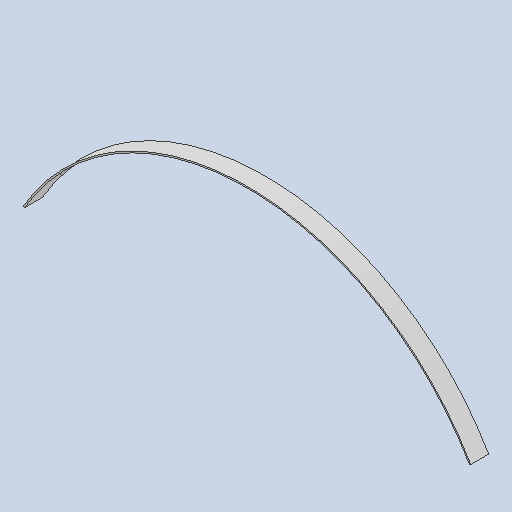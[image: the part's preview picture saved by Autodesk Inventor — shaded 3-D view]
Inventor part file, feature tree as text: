
AUTODESK INVENTOR PART (.ipt)
format: ipt  version: 2025 (Build 290162010, 162A)  size: 294,912 bytes
history: native  units: mm
features: sheet_metal_op x3, other x2, sketch x1
ambient origin geometry x8: Origin, YZ Plane, XZ Plane, XY Plane, X Axis, Y Axis, Z Axis, Center Point
bodies: Body1 (feature_tree)
feature tree (6):
  sheet_metal_op  "Contour Flange1"
  sketch  "Sketch1"  dims[d28=720.0mm d30=120.0deg d31=2.0mm d32=2.0mm d33=1.0mm d34=4.0mm d35=2.0mm d36=25.0mm d37=2.0mm d38=2.0mm d39=8.0mm d40=2.0mm d41=2.0mm]
  other  "Plate2"
  sheet_metal_op  "Bend1"
  sheet_metal_op  "Corner1"
  other  "Definition1"
